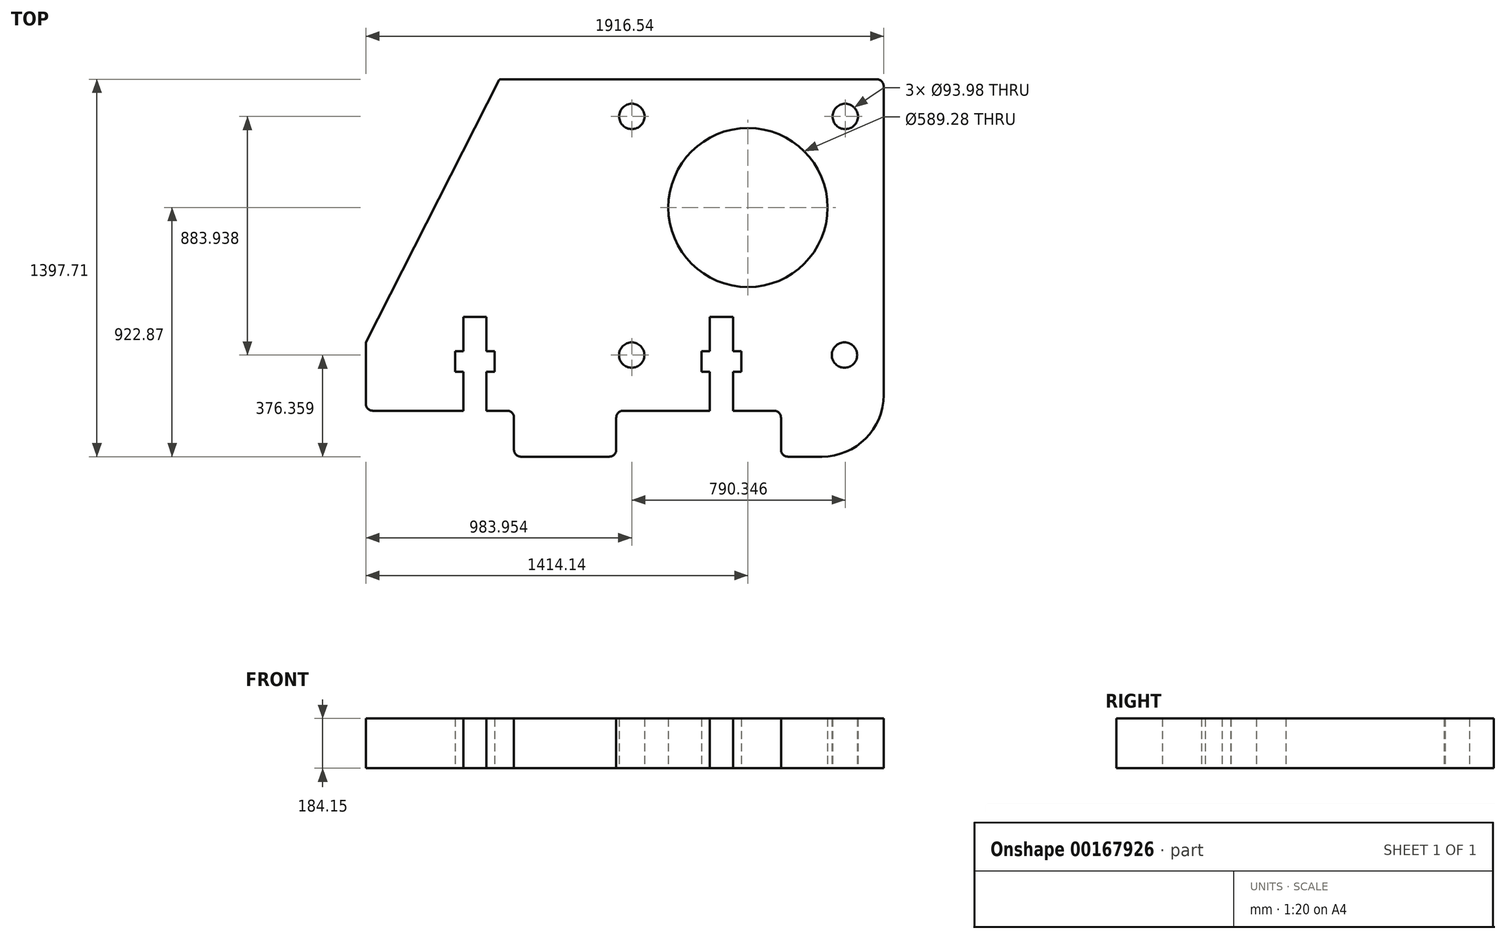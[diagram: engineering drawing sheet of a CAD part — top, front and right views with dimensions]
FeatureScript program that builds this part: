
annotation { "Feature Type Name" : "Feature", "Feature Type Description" : "" }
export const myFeature = defineFeature(function(context is Context, id is Id, definition is map)
    precondition{}
    {
        {
            var Q0;
            Q0=qCreatedBy(makeId("Top.planeOp"),FACE);
            var sketch = newSketch(context, id + "F0", { "sketchPlane" : qUnion([Q0])});
            skLineSegment(sketch, "E0", {"start": v(539.2, 598.23) * mm, "end": v(-854.32, 598.23) * mm});
            skLineSegment(sketch, "E1", {"start": v(-859.39, 595.12) * mm, "end": v(-1351.95, -375.3) * mm});
            skLineSegment(sketch, "E2", {"start": v(-1351.95, -375.3) * mm, "end": v(-1351.95, -603.9) * mm});
            skLineSegment(sketch, "E3", {"start": v(-1326.55, -629.3) * mm, "end": v(-991.27, -629.3) * mm});
            skLineSegment(sketch, "E4", {"start": v(-991.27, -629.3) * mm, "end": v(-991.27, -484.52) * mm});
            skLineSegment(sketch, "E5", {"start": v(-991.27, -484.52) * mm, "end": v(-1021.75, -484.52) * mm});
            skLineSegment(sketch, "E6", {"start": v(-1021.75, -484.52) * mm, "end": v(-1021.75, -408.32) * mm});
            skLineSegment(sketch, "E7", {"start": v(-1021.75, -408.32) * mm, "end": v(-991.27, -408.32) * mm});
            skLineSegment(sketch, "E8", {"start": v(-991.27, -408.32) * mm, "end": v(-991.27, -281.32) * mm});
            skLineSegment(sketch, "E9", {"start": v(-991.27, -281.32) * mm, "end": v(-905.93, -281.32) * mm});
            skLineSegment(sketch, "E10", {"start": v(-905.93, -281.32) * mm, "end": v(-905.93, -408.32) * mm});
            skLineSegment(sketch, "E11", {"start": v(-905.93, -408.32) * mm, "end": v(-875.45, -408.32) * mm});
            skLineSegment(sketch, "E12", {"start": v(-875.45, -408.32) * mm, "end": v(-875.45, -484.52) * mm});
            skLineSegment(sketch, "E13", {"start": v(-875.45, -484.52) * mm, "end": v(-905.93, -484.52) * mm});
            skLineSegment(sketch, "E14", {"start": v(-905.93, -484.52) * mm, "end": v(-905.93, -629.3) * mm});
            skLineSegment(sketch, "E15", {"start": v(-905.93, -629.3) * mm, "end": v(-829.14, -629.3) * mm});
            skLineSegment(sketch, "E16", {"start": v(-803.74, -654.7) * mm, "end": v(-803.74, -774.08) * mm});
            skLineSegment(sketch, "E17", {"start": v(-778.34, -799.48) * mm, "end": v(-450.68, -799.48) * mm});
            skLineSegment(sketch, "E18", {"start": v(-425.28, -774.08) * mm, "end": v(-425.28, -654.7) * mm});
            skLineSegment(sketch, "E19", {"start": v(-399.88, -629.3) * mm, "end": v(-78.65, -629.3) * mm});
            skLineSegment(sketch, "E20", {"start": v(-78.65, -629.3) * mm, "end": v(-78.65, -484.52) * mm});
            skLineSegment(sketch, "E21", {"start": v(-78.65, -484.52) * mm, "end": v(-109.13, -484.52) * mm});
            skLineSegment(sketch, "E22", {"start": v(-109.13, -484.52) * mm, "end": v(-109.13, -408.32) * mm});
            skLineSegment(sketch, "E23", {"start": v(-109.13, -408.32) * mm, "end": v(-78.65, -408.32) * mm});
            skLineSegment(sketch, "E24", {"start": v(-78.65, -408.32) * mm, "end": v(-78.65, -281.32) * mm});
            skLineSegment(sketch, "E25", {"start": v(-78.65, -281.32) * mm, "end": v(6.7, -281.32) * mm});
            skLineSegment(sketch, "E26", {"start": v(6.7, -281.32) * mm, "end": v(6.7, -408.32) * mm});
            skLineSegment(sketch, "E27", {"start": v(6.7, -408.32) * mm, "end": v(37.18, -408.32) * mm});
            skLineSegment(sketch, "E28", {"start": v(37.18, -408.32) * mm, "end": v(37.18, -484.52) * mm});
            skLineSegment(sketch, "E29", {"start": v(37.18, -484.52) * mm, "end": v(6.7, -484.52) * mm});
            skLineSegment(sketch, "E30", {"start": v(6.7, -484.52) * mm, "end": v(6.7, -629.3) * mm});
            skLineSegment(sketch, "E31", {"start": v(6.7, -629.3) * mm, "end": v(159.1, -629.3) * mm});
            skLineSegment(sketch, "E32", {"start": v(184.5, -654.7) * mm, "end": v(184.5, -774.08) * mm});
            skLineSegment(sketch, "E33", {"start": v(209.9, -799.48) * mm, "end": v(565.5, -799.48) * mm});
            skLineSegment(sketch, "E34", {"start": v(564.6, -570.88) * mm, "end": v(564.6, 572.83) * mm});
            skCircle(sketch, "E35", {"center": v(62.2, 123.4) * mm, "radius": 294.64 * mm});
            skCircle(sketch, "E36", {"center": v(-367.59, 460.82) * mm, "radius": 47 * mm});
            skCircle(sketch, "E37", {"center": v(422.35, 460.82) * mm, "radius": 47 * mm});
            skCircle(sketch, "E38", {"center": v(419.59, -423.1) * mm, "radius": 46.99 * mm});
            skPoint(sketch, "E39.newPointA", {"position": v(525.88, -799.48) * mm});
            skPoint(sketch, "E39.newPointB", {"position": v(564.6, -798.77) * mm});
            skArc(sketch, "E39.filletArc", {"start": v(336, -799.48) * mm, "mid": v(497.63, -732.53) * mm, "end": v(564.6, -570.88) * mm});
            skPoint(sketch, "E40.visualSharp", {"position": v(-857.8, 598.23) * mm});
            skArc(sketch, "E40.filletArc", {"start": v(-854.32, 598.23) * mm, "mid": v(-857.3, 597.4) * mm, "end": v(-859.39, 595.12) * mm});
            skPoint(sketch, "E41.visualSharp", {"position": v(-1351.95, -629.3) * mm});
            skArc(sketch, "E41.filletArc", {"start": v(-1351.95, -603.9) * mm, "mid": v(-1344.51, -621.87) * mm, "end": v(-1326.55, -629.3) * mm});
            skPoint(sketch, "E42.visualSharp", {"position": v(-803.74, -629.3) * mm});
            skArc(sketch, "E42.filletArc", {"start": v(-803.74, -654.7) * mm, "mid": v(-811.18, -636.74) * mm, "end": v(-829.14, -629.3) * mm});
            skPoint(sketch, "E43.visualSharp", {"position": v(-803.74, -799.48) * mm});
            skArc(sketch, "E43.filletArc", {"start": v(-803.74, -774.08) * mm, "mid": v(-796.3, -792.05) * mm, "end": v(-778.34, -799.48) * mm});
            skPoint(sketch, "E44.visualSharp", {"position": v(-425.28, -799.48) * mm});
            skArc(sketch, "E44.filletArc", {"start": v(-450.68, -799.48) * mm, "mid": v(-432.72, -792.05) * mm, "end": v(-425.28, -774.08) * mm});
            skPoint(sketch, "E45.visualSharp", {"position": v(-425.28, -629.3) * mm});
            skArc(sketch, "E45.filletArc", {"start": v(-399.88, -629.3) * mm, "mid": v(-417.84, -636.74) * mm, "end": v(-425.28, -654.7) * mm});
            skPoint(sketch, "E46.visualSharp", {"position": v(184.5, -629.3) * mm});
            skArc(sketch, "E46.filletArc", {"start": v(184.5, -654.7) * mm, "mid": v(177.06, -636.74) * mm, "end": v(159.1, -629.3) * mm});
            skPoint(sketch, "E47.visualSharp", {"position": v(184.5, -799.48) * mm});
            skArc(sketch, "E47.filletArc", {"start": v(184.5, -774.08) * mm, "mid": v(191.93, -792.05) * mm, "end": v(209.9, -799.48) * mm});
            skPoint(sketch, "E48.visualSharp", {"position": v(564.6, 598.23) * mm});
            skArc(sketch, "E48.filletArc", {"start": v(564.6, 572.83) * mm, "mid": v(557.15, 590.8) * mm, "end": v(539.2, 598.23) * mm});
            skCircle(sketch, "E49", {"center": v(-368, -423.12) * mm, "radius": 47 * mm});
            skLineSegment(sketch, "E50", {"start": v(-367.59, 460.82) * mm, "end": v(-367.59, 460.82) * mm});
            skLineSegment(sketch, "E51", {"start": v(-367.59, 460.82) * mm, "end": v(419.59, -423.1) * mm, "construction": true});
            skLineSegment(sketch, "E52", {"start": v(-368.86, -424.44) * mm, "end": v(422.35, 460.82) * mm, "construction": true});
            skSolve(sketch);
        }
        {
            var Q0;
            Q0=makeQuery(id+"F0.imprint","IMPRINT",FACE,{"disambiguationData":[TD([[makeQuery(id+"F0.imprint","IMPRINT",EDGE,{"derivedFrom":sQuery(id+"F0.wireOp",EDGE,"E0")}),1.0]])]});
            extrude(context, id + "F1", {"entities" : qUnion([Q0]), "depth" : 184.15 * mm});
        }
    });
